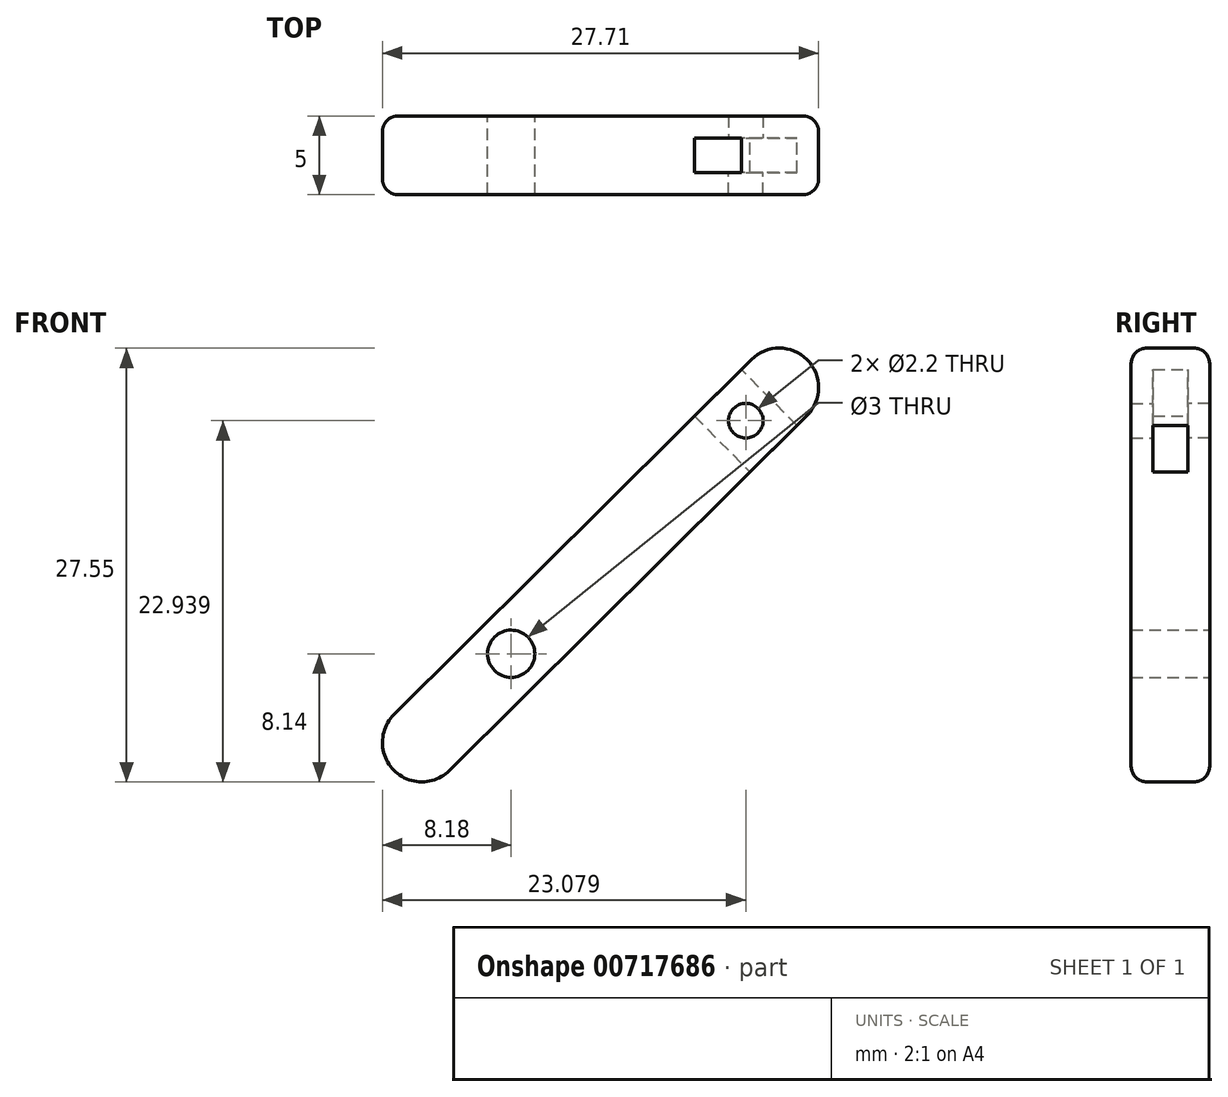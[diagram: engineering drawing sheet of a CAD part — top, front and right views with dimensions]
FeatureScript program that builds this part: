
annotation { "Feature Type Name" : "Feature", "Feature Type Description" : "" }
export const myFeature = defineFeature(function(context is Context, id is Id, definition is map)
    precondition{}
    {
        {
            var Q0;
            Q0=qCreatedBy(makeId("Front.planeOp"),FACE);
            var sketch = newSketch(context, id + "F0", { "sketchPlane" : qUnion([Q0])});
            skLineSegment(sketch, "E0.bottom", {"start": v(-3.91, -7.41) * mm, "end": v(18.79, 15.14) * mm});
            skLineSegment(sketch, "E0.top", {"start": v(-7.44, -3.86) * mm, "end": v(15.27, 18.69) * mm});
            skPoint(sketch, "E0.middle", {"position": v(5.68, 5.64) * mm});
            skArc(sketch, "E1", {"start": v(-7.44, -3.86) * mm, "mid": v(-7.45, -7.4) * mm, "end": v(-3.91, -7.41) * mm});
            skArc(sketch, "E2", {"start": v(18.79, 15.14) * mm, "mid": v(18.8, 18.67) * mm, "end": v(15.27, 18.69) * mm});
            skCircle(sketch, "E3", {"center": v(0, 0) * mm, "radius": 10.5 * mm, "construction": true});
            skCircle(sketch, "E4", {"center": v(0, 0) * mm, "radius": 1.5 * mm});
            skLineSegment(sketch, "E5", {"start": v(-5.68, -5.64) * mm, "end": v(17.03, 16.91) * mm, "construction": true});
            skLineSegment(sketch, "E6", {"start": v(-7.45, -7.4) * mm, "end": v(-7.45, -10.4) * mm, "construction": true});
            skLineSegment(sketch, "E7", {"start": v(-7.45, -10.4) * mm, "end": v(-1.45, -10.4) * mm, "construction": true});
            skLineSegment(sketch, "E8", {"start": v(0, 0) * mm, "end": v(0, -10.5) * mm, "construction": true});
            skSolve(sketch);
        }
        {
            var Q0;
            Q0=makeQuery(id+"F0.imprint","IMPRINT",FACE,{"disambiguationData":[TD([[makeQuery(id+"F0.imprint","IMPRINT",EDGE,{"derivedFrom":sQuery(id+"F0.wireOp",EDGE,"E0.bottom")}),1.0]])]});
            var Q1;
            Q1=makeQuery(id+"F0.imprint","IMPRINT",FACE,{"disambiguationData":[TD([[makeQuery(id+"F0.imprint","IMPRINT",EDGE,{"derivedFrom":sQuery(id+"F0.wireOp",EDGE,"E4")}),1.0]])]});
            extrude(context, id + "F1", {"entities" : qUnion([Q0, Q1]), "endBound" : BoundingType.SYMMETRIC, "depth" : 5 * mm, "offsetDistance" : 25 * mm});
        }
        {
            var Q0;
            Q0=makeQuery(id+"F0.imprint","IMPRINT",FACE,{"disambiguationData":[TD([[makeQuery(id+"F0.imprint","IMPRINT",EDGE,{"derivedFrom":sQuery(id+"F0.wireOp",EDGE,"E4")}),1.0]])]});
            extrude(context, id + "F2", {"entities" : qUnion([Q0]), "operationType" : NewBodyOperationType.REMOVE, "endBound" : BoundingType.SYMMETRIC, "depth" : 10 * mm, "offsetDistance" : 25 * mm});
        }
        {
            var Q0;
            Q0=makeQuery(id+"F1.opExtrude","CAP_EDGE",EDGE,{"disambiguationData":[OSD([sQuery(id+"F0.wireOp",EDGE,"E0.top")])],"isStart":false});
            var Q1;
            Q1=makeQuery(id+"F1.opExtrude","CAP_EDGE",EDGE,{"disambiguationData":[OSD([sQuery(id+"F0.wireOp",EDGE,"E0.top")])],"isStart":true});
            fillet(context, id + "F3", {"entities" : qUnion([Q0, Q1]), "radius" : 1 * mm, "tangentPropagation" : true, "allowEdgeOverflow" : false});
        }
        {
            var Q0;
            Q0=qCreatedBy(makeId("Front.planeOp"),FACE);
            var sketch = newSketch(context, id + "F4", { "sketchPlane" : qUnion([Q0])});
            skArc(sketch, "E9.0", {"start": v(-3.91, -7.41) * mm, "mid": v(-7.45, -7.4) * mm, "end": v(-7.44, -3.86) * mm});
            skLineSegment(sketch, "E10.0", {"start": v(-7.44, -3.86) * mm, "end": v(15.27, 18.69) * mm});
            skLineSegment(sketch, "E11.0", {"start": v(18.79, 15.14) * mm, "end": v(-3.91, -7.41) * mm});
            skSolve(sketch);
        }
        {
            var Q0;
            Q0=qCreatedBy(makeId("Front.planeOp"),FACE);
            var sketch = newSketch(context, id + "F5", { "sketchPlane" : qUnion([Q0])});
            skCircle(sketch, "E12.cCircle", {"center": v(14.9, 14.8) * mm, "radius": 2.1 * mm, "construction": true});
            skLineSegment(sketch, "E12.0", {"start": v(16.6, 13.08) * mm, "end": v(14.26, 12.46) * mm});
            skLineSegment(sketch, "E12.1", {"start": v(14.26, 12.46) * mm, "end": v(12.56, 14.18) * mm});
            skLineSegment(sketch, "E12.2", {"start": v(12.56, 14.18) * mm, "end": v(13.2, 16.52) * mm});
            skLineSegment(sketch, "E12.3", {"start": v(13.2, 16.52) * mm, "end": v(15.53, 17.14) * mm});
            skLineSegment(sketch, "E12.4", {"start": v(15.53, 17.14) * mm, "end": v(17.24, 15.42) * mm});
            skLineSegment(sketch, "E12.5", {"start": v(17.24, 15.42) * mm, "end": v(16.6, 13.08) * mm});
            skPoint(sketch, "E12.0.midPoint", {"position": v(15.44, 12.77) * mm});
            skLineSegment(sketch, "E13", {"start": v(14.9, 14.8) * mm, "end": v(0, 0) * mm, "construction": true});
            skLineSegment(sketch, "E14", {"start": v(11.65, 15.1) * mm, "end": v(15.17, 11.55) * mm});
            skLineSegment(sketch, "E15", {"start": v(15.17, 11.55) * mm, "end": v(18.15, 14.5) * mm});
            skLineSegment(sketch, "E16", {"start": v(18.15, 14.5) * mm, "end": v(14.63, 18.05) * mm});
            skLineSegment(sketch, "E17", {"start": v(14.63, 18.05) * mm, "end": v(11.65, 15.1) * mm});
            skSolve(sketch);
        }
        {
            var Q0;
            Q0 = qSketchRegion(id + "F5", true);
            extrude(context, id + "F6", {"entities" : qUnion([Q0]), "operationType" : NewBodyOperationType.REMOVE, "endBound" : BoundingType.SYMMETRIC, "depth" : 2.2 * mm, "offsetDistance" : 25 * mm});
        }
        {
            var Q0;
            Q0=sQuery(id+"F5.wireOp",VERTEX,"E13.start");
            var Q1;
            Q1=makeQuery(id+"F1.opExtrude","SWEPT_BODY",BODY,{"disambiguationData":[OSD([sQuery(id+"F0.wireOp",EDGE,"E0.bottom"),sQuery(id+"F0.wireOp",EDGE,"E0.top"),sQuery(id+"F0.wireOp",EDGE,"E1"),sQuery(id+"F0.wireOp",EDGE,"E2")])]});
            hole(context, id + "F7", {"style" : HoleStyle.SIMPLE, "endStyle" : HoleEndStyle.THROUGH, "holeDiameter" : 2.2 * mm, "majorDiameter" : 5 * mm, "isTappedThrough" : true, "tappedDepth" : 2.3 * mm, "tapClearance" : 3, "startFromSketch" : true, "locations" : qUnion([Q0]), "scope" : qUnion([Q1])});
        }
        {
            var Q0;
            Q0=sQuery(id+"F5.wireOp",VERTEX,"E12.cCircle.center");
            var Q1;
            Q1=makeQuery(id+"F1.opExtrude","SWEPT_BODY",BODY,{"disambiguationData":[OSD([sQuery(id+"F0.wireOp",EDGE,"E0.bottom"),sQuery(id+"F0.wireOp",EDGE,"E0.top"),sQuery(id+"F0.wireOp",EDGE,"E1"),sQuery(id+"F0.wireOp",EDGE,"E2")])]});
            hole(context, id + "F8", {"style" : HoleStyle.SIMPLE, "endStyle" : HoleEndStyle.THROUGH, "oppositeDirection" : true, "holeDiameter" : 2.2 * mm, "majorDiameter" : 5 * mm, "isTappedThrough" : true, "tappedDepth" : 2.3 * mm, "tapClearance" : 3, "startFromSketch" : true, "locations" : qUnion([Q0]), "scope" : qUnion([Q1])});
        }
    });
